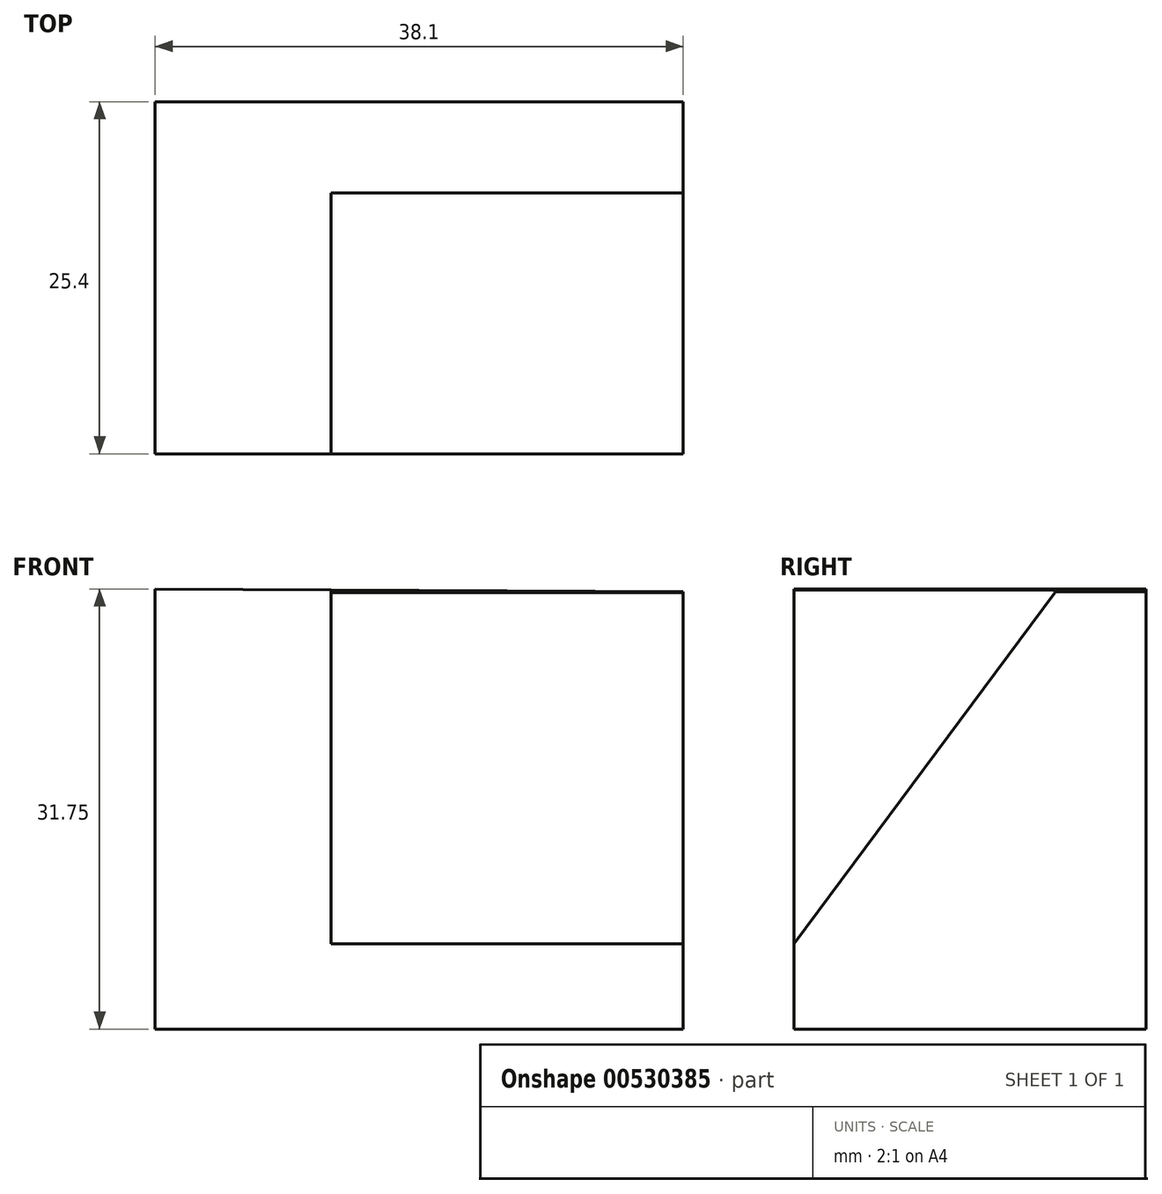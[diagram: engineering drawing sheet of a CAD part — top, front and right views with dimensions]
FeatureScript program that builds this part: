
annotation { "Feature Type Name" : "Feature", "Feature Type Description" : "" }
export const myFeature = defineFeature(function(context is Context, id is Id, definition is map)
    precondition{}
    {
        {
            var Q0;
            Q0=qCreatedBy(makeId("Front.planeOp"),FACE);
            var sketch = newSketch(context, id + "F0", { "sketchPlane" : qUnion([Q0])});
            skLineSegment(sketch, "E0", {"start": v(-38.1, 31.75) * mm, "end": v(-38.1, 0) * mm});
            skLineSegment(sketch, "E1", {"start": v(-38.1, 0) * mm, "end": v(0, 0) * mm});
            skLineSegment(sketch, "E2", {"start": v(0, 0) * mm, "end": v(0, 31.56) * mm});
            skLineSegment(sketch, "E3", {"start": v(0, 31.56) * mm, "end": v(-38.1, 31.75) * mm});
            skSolve(sketch);
        }
        {
            var Q0;
            Q0=makeQuery(id+"F0.imprint","IMPRINT",FACE,{"disambiguationData":[TD([[makeQuery(id+"F0.imprint","IMPRINT",EDGE,{"derivedFrom":sQuery(id+"F0.wireOp",EDGE,"E0")}),1.0]])]});
            extrude(context, id + "F1", {"entities" : qUnion([Q0]), "depth" : 25.4 * mm, "offsetDistance" : 25.4 * mm});
        }
        {
            var Q0;
            Q0=qCreatedBy(makeId("Right.planeOp"),FACE);
            var sketch = newSketch(context, id + "F2", { "sketchPlane" : qUnion([Q0])});
            skLineSegment(sketch, "E4", {"start": v(-6.58, 31.48) * mm, "end": v(-25.44, 6.08) * mm});
            skLineSegment(sketch, "E5", {"start": v(-6.58, 31.48) * mm, "end": v(-25.63, 31.48) * mm});
            skLineSegment(sketch, "E6", {"start": v(-25.63, 31.48) * mm, "end": v(-25.44, 6.08) * mm});
            skLineSegment(sketch, "E7", {"start": v(-25.44, 6.08) * mm, "end": v(-25.4, 0) * mm});
            skLineSegment(sketch, "E8", {"start": v(-25.4, 0) * mm, "end": v(0, 0) * mm});
            skLineSegment(sketch, "E9", {"start": v(0, 0) * mm, "end": v(-0.23, 31.48) * mm});
            skLineSegment(sketch, "E10", {"start": v(-0.23, 31.48) * mm, "end": v(-6.58, 31.48) * mm});
            skSolve(sketch);
        }
        {
            var Q0;
            Q0=makeQuery(id+"F2.imprint","IMPRINT",FACE,{"disambiguationData":[TD([[makeQuery(id+"F2.imprint","IMPRINT",EDGE,{"derivedFrom":sQuery(id+"F2.wireOp",EDGE,"E4")}),-1.0]])]});
            extrude(context, id + "F3", {"entities" : qUnion([Q0]), "operationType" : NewBodyOperationType.REMOVE, "oppositeDirection" : true, "depth" : 25.4 * mm, "offsetDistance" : 25.4 * mm});
        }
        {
            var Q0;
            Q0=makeQuery(id+"F3.boolean.opBoolean","COPY",FACE,{"derivedFrom":makeQuery(id+"F3.opExtrude","SWEPT_FACE",FACE,{"disambiguationData":[OSD([sQuery(id+"F2.wireOp",EDGE,"E5")])]})});
            extrude(context, id + "F4", {"entities" : qUnion([Q0]), "operationType" : NewBodyOperationType.REMOVE, "endBound" : BoundingType.THROUGH_ALL, "oppositeDirection" : true, "depth" : 25.4 * mm, "offsetDistance" : 25.4 * mm});
        }
    });
